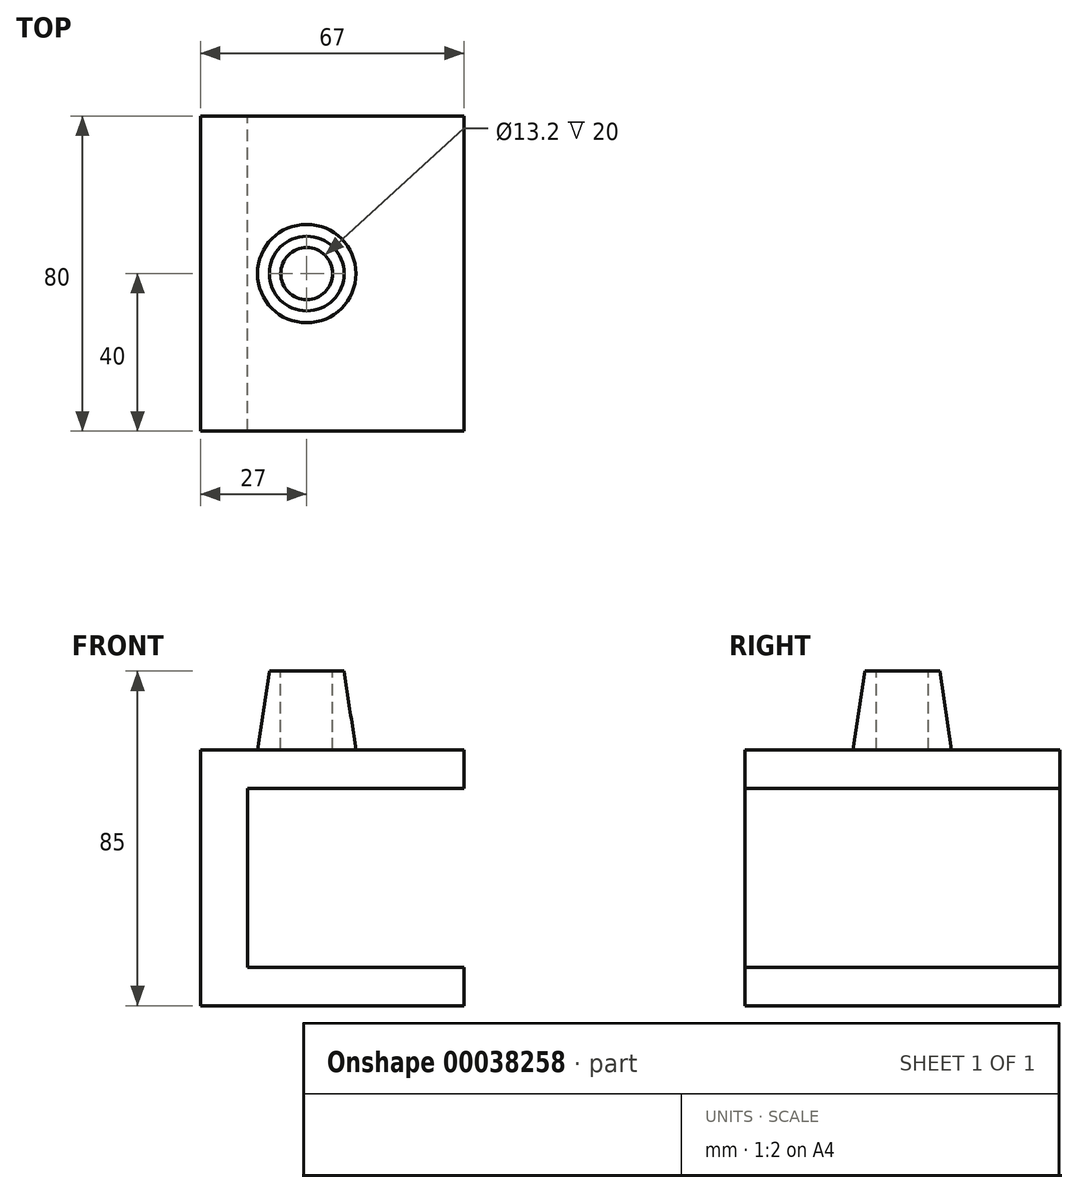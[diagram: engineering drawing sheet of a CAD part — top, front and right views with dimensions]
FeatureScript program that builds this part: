
annotation { "Feature Type Name" : "Feature", "Feature Type Description" : "" }
export const myFeature = defineFeature(function(context is Context, id is Id, definition is map)
    precondition{}
    {
        {
            var Q0;
            Q0=qCreatedBy(makeId("Right.planeOp"),FACE);
            var sketch = newSketch(context, id + "F0", { "sketchPlane" : qUnion([Q0])});
            skLineSegment(sketch, "E0.rect.bottom", {"start": v(40, 32.5) * mm, "end": v(-40, 32.5) * mm});
            skLineSegment(sketch, "E0.rect.top", {"start": v(40, -32.5) * mm, "end": v(-40, -32.5) * mm});
            skLineSegment(sketch, "E0.rect.left", {"start": v(40, 32.5) * mm, "end": v(40, -32.5) * mm});
            skLineSegment(sketch, "E0.rect.right", {"start": v(-40, 32.5) * mm, "end": v(-40, -32.5) * mm});
            skPoint(sketch, "E0.rect.middle", {"position": v(0, 0) * mm});
            skSolve(sketch);
        }
        {
            var Q0;
            Q0 = qSketchRegion(id + "F0", true);
            extrude(context, id + "F1", {"entities" : qUnion([Q0]), "oppositeDirection" : true, "depth" : 12 * mm});
        }
        {
            var Q0;
            Q0=makeQuery(id+"F1.opExtrude","CAP_FACE",FACE,{"disambiguationData":[OSD([sQuery(id+"F0.wireOp",EDGE,"E0.rect.bottom"),sQuery(id+"F0.wireOp",EDGE,"E0.rect.top"),sQuery(id+"F0.wireOp",EDGE,"E0.rect.left"),sQuery(id+"F0.wireOp",EDGE,"E0.rect.right")])],"isStart":true});
            var sketch = newSketch(context, id + "F2", { "sketchPlane" : qUnion([Q0])});
            skLineSegment(sketch, "E1", {"start": v(-40, 32.5) * mm, "end": v(-40, 22.75) * mm});
            skLineSegment(sketch, "E2", {"start": v(-40, 22.75) * mm, "end": v(40, 22.75) * mm});
            skLineSegment(sketch, "E3", {"start": v(40, 22.75) * mm, "end": v(40, 32.5) * mm});
            skLineSegment(sketch, "E4", {"start": v(40, 32.5) * mm, "end": v(-40, 32.5) * mm});
            skLineSegment(sketch, "E5.MirrorCS", {"start": v(-40, -22.75) * mm, "end": v(40, -22.75) * mm});
            skLineSegment(sketch, "E6.MirrorCS", {"start": v(-40, -32.5) * mm, "end": v(-40, -22.75) * mm});
            skLineSegment(sketch, "E7.MirrorCS", {"start": v(40, -32.5) * mm, "end": v(-40, -32.5) * mm});
            skLineSegment(sketch, "E8.MirrorCS", {"start": v(40, -22.75) * mm, "end": v(40, -32.5) * mm});
            skSolve(sketch);
        }
        {
            var Q0;
            Q0 = qSketchRegion(id + "F2", true);
            extrude(context, id + "F3", {"entities" : qUnion([Q0]), "operationType" : NewBodyOperationType.ADD, "depth" : 55 * mm});
        }
        {
            var Q0;
            Q0=makeQuery(id+"F3.boolean.opBoolean","MERGE",FACE,{"derivedFrom":[makeQuery(id+"F1.opExtrude","SWEPT_FACE",FACE,{"disambiguationData":[OSD([sQuery(id+"F0.wireOp",EDGE,"E0.rect.bottom")])]}),makeQuery(id+"F3.opExtrude","SWEPT_FACE",FACE,{"disambiguationData":[OSD([sQuery(id+"F2.wireOp",EDGE,"E4")])]})]});
            var sketch = newSketch(context, id + "F4", { "sketchPlane" : qUnion([Q0])});
            skLineSegment(sketch, "E9", {"start": v(0, 0) * mm, "end": v(15, 0) * mm, "construction": true});
            skCircle(sketch, "E10", {"center": v(15, 0) * mm, "radius": 12.5 * mm});
            skSolve(sketch);
        }
        {
            var Q0;
            Q0=makeQuery(id+"F4.imprint","IMPRINT",FACE,{"disambiguationData":[TD([[makeQuery(id+"F4.imprint","IMPRINT",EDGE,{"derivedFrom":sQuery(id+"F4.wireOp",EDGE,"E10")}),-1.0]])]});
            cPlane(context, id + "F5", {"entities" : qUnion([Q0]), "cplaneType" : CPlaneType.OFFSET, "offset" : 20 * mm, "width" : 152.4 * mm, "height" : 152.4 * mm});
        }
        {
            var Q0;
            Q0=qCreatedBy(id+"F5.planeOp",FACE);
            var sketch = newSketch(context, id + "F6", { "sketchPlane" : qUnion([Q0])});
            skCircle(sketch, "E11", {"center": v(15, 0) * mm, "radius": 9.5 * mm});
            skSolve(sketch);
        }
        {
            var Q0;
            Q0=makeQuery(id+"F4.imprint","IMPRINT",FACE,{"disambiguationData":[TD([[makeQuery(id+"F4.imprint","IMPRINT",EDGE,{"derivedFrom":sQuery(id+"F4.wireOp",EDGE,"E10")}),1.0]])]});
            var Q1;
            Q1=makeQuery(id+"F6.imprint","IMPRINT",FACE,{"disambiguationData":[TD([[makeQuery(id+"F6.imprint","IMPRINT",EDGE,{"derivedFrom":sQuery(id+"F6.wireOp",EDGE,"E11")}),1.0]])]});
            var Q2;
            Q2=sQuery(id+"F4.wireOp",EDGE,"E10");
            var Q3;
            Q3=sQuery(id+"F6.wireOp",EDGE,"E11");
            loft(context, id + "F7", {"sheetProfilesArray" : [{ "sheetProfileEntities" : qUnion([Q0]) }, { "sheetProfileEntities" : qUnion([Q1]) }], "wireProfilesArray" : [{ "wireProfileEntities" : qUnion([Q2]) }, { "wireProfileEntities" : qUnion([Q3]) }]});
        }
        {
            var Q0;
            Q0=makeQuery(id+"F7.opLoft","CAP_FACE",FACE,{"disambiguationData":[OSD([makeQuery(id+"F6.imprint","IMPRINT",FACE,{"disambiguationData":[TD([[makeQuery(id+"F6.imprint","IMPRINT",EDGE,{"derivedFrom":sQuery(id+"F6.wireOp",EDGE,"E11")}),1.0]])]})])],"isStart":true});
            var sketch = newSketch(context, id + "F8", { "sketchPlane" : qUnion([Q0])});
            skCircle(sketch, "E12", {"center": v(15, 0) * mm, "radius": 6.55 * mm});
            skSolve(sketch);
        }
        {
            var Q0;
            Q0=sQuery(id+"F8.wireOp",VERTEX,"E12.center");
            var Q1;
            Q1=makeQuery(id+"F7.opLoft","SWEPT_BODY",BODY,{"disambiguationData":[OSD([makeQuery(id+"F4.imprint","IMPRINT",FACE,{"disambiguationData":[TD([[makeQuery(id+"F4.imprint","IMPRINT",EDGE,{"derivedFrom":sQuery(id+"F4.wireOp",EDGE,"E10")}),1.0]])]}),makeQuery(id+"F6.imprint","IMPRINT",FACE,{"disambiguationData":[TD([[makeQuery(id+"F6.imprint","IMPRINT",EDGE,{"derivedFrom":sQuery(id+"F6.wireOp",EDGE,"E11")}),1.0]])]})])]});
            hole(context, id + "F9", {"style" : HoleStyle.SIMPLE, "holeDiameter" : 13.2 * mm, "endStyle" : HoleEndStyle.BLIND, "holeDepth" : 20 * mm, "locations" : qUnion([Q0]), "scope" : qUnion([Q1])});
        }
    });
